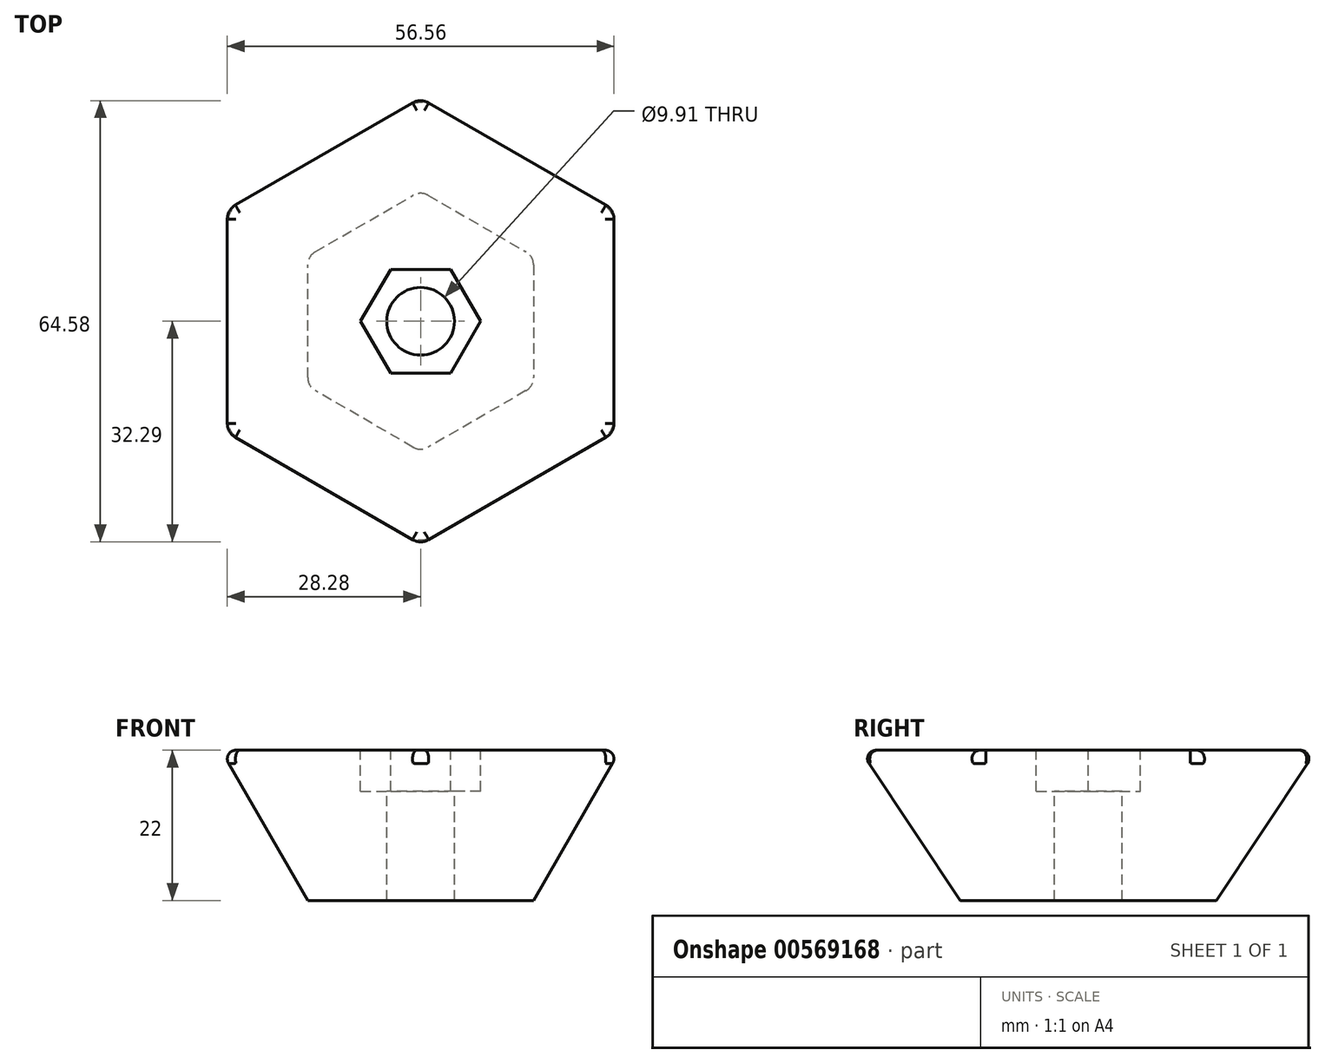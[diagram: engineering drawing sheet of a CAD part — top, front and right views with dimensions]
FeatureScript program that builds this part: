
annotation { "Feature Type Name" : "Feature", "Feature Type Description" : "" }
export const myFeature = defineFeature(function(context is Context, id is Id, definition is map)
    precondition{}
    {
        {
            var Q0;
            Q0=qCreatedBy(makeId("Top.planeOp"),FACE);
            var sketch = newSketch(context, id + "F0", { "sketchPlane" : qUnion([Q0])});
            skCircle(sketch, "E0.cCircle", {"center": v(0, 0) * mm, "radius": 29.21 * mm, "construction": true});
            skLineSegment(sketch, "E0.0", {"start": v(29.21, 16.86) * mm, "end": v(29.21, -16.86) * mm});
            skLineSegment(sketch, "E0.1", {"start": v(29.21, -16.86) * mm, "end": v(0, -33.73) * mm});
            skLineSegment(sketch, "E0.2", {"start": v(0, -33.73) * mm, "end": v(-29.2, -16.86) * mm});
            skLineSegment(sketch, "E0.3", {"start": v(-29.2, -16.86) * mm, "end": v(-29.21, 16.86) * mm});
            skLineSegment(sketch, "E0.4", {"start": v(-29.21, 16.86) * mm, "end": v(0, 33.73) * mm});
            skLineSegment(sketch, "E0.5", {"start": v(0, 33.73) * mm, "end": v(29.21, 16.86) * mm});
            skPoint(sketch, "E0.0.midPoint", {"position": v(29.21, 0) * mm});
            skSolve(sketch);
        }
        {
            var Q0;
            Q0 = qSketchRegion(id + "F0", true);
            extrude(context, id + "F1", {"entities" : qUnion([Q0]), "depth" : 22 * mm, "offsetDistance" : 25.4 * mm});
        }
        {
            var Q0;
            Q0=makeQuery(id+"F1.opExtrude","CAP_FACE",FACE,{"disambiguationData":[OSD([sQuery(id+"F0.wireOp",EDGE,"E0.0"),sQuery(id+"F0.wireOp",EDGE,"E0.1"),sQuery(id+"F0.wireOp",EDGE,"E0.2"),sQuery(id+"F0.wireOp",EDGE,"E0.3"),sQuery(id+"F0.wireOp",EDGE,"E0.4"),sQuery(id+"F0.wireOp",EDGE,"E0.5")])],"isStart":false});
            var sketch = newSketch(context, id + "F2", { "sketchPlane" : qUnion([Q0])});
            skCircle(sketch, "E1.cCircle", {"center": v(0, 0) * mm, "radius": 7.6 * mm, "construction": true});
            skLineSegment(sketch, "E1.0", {"start": v(-4.4, 7.6) * mm, "end": v(4.4, 7.6) * mm});
            skLineSegment(sketch, "E1.1", {"start": v(4.4, 7.6) * mm, "end": v(8.78, 0) * mm});
            skLineSegment(sketch, "E1.2", {"start": v(8.78, 0) * mm, "end": v(4.4, -7.6) * mm});
            skLineSegment(sketch, "E1.3", {"start": v(4.4, -7.6) * mm, "end": v(-4.4, -7.6) * mm});
            skLineSegment(sketch, "E1.4", {"start": v(-4.4, -7.6) * mm, "end": v(-8.78, 0) * mm});
            skLineSegment(sketch, "E1.5", {"start": v(-8.78, 0) * mm, "end": v(-4.4, 7.6) * mm});
            skPoint(sketch, "E1.0.midPoint", {"position": v(0, 7.6) * mm});
            skSolve(sketch);
        }
        {
            var Q0;
            Q0 = qSketchRegion(id + "F2", true);
            extrude(context, id + "F3", {"entities" : qUnion([Q0]), "operationType" : NewBodyOperationType.REMOVE, "oppositeDirection" : true, "depth" : 6 * mm, "offsetDistance" : 25.4 * mm});
        }
        {
            var Q0;
            Q0=makeQuery(id+"F3.boolean.opBoolean","COPY",FACE,{"derivedFrom":makeQuery(id+"F3.opExtrude","CAP_FACE",FACE,{"disambiguationData":[OSD([sQuery(id+"F2.wireOp",EDGE,"E1.0"),sQuery(id+"F2.wireOp",EDGE,"E1.1"),sQuery(id+"F2.wireOp",EDGE,"E1.2"),sQuery(id+"F2.wireOp",EDGE,"E1.3"),sQuery(id+"F2.wireOp",EDGE,"E1.4"),sQuery(id+"F2.wireOp",EDGE,"E1.5")])],"isStart":false})});
            var sketch = newSketch(context, id + "F4", { "sketchPlane" : qUnion([Q0])});
            skCircle(sketch, "E2", {"center": v(0, 0) * mm, "radius": 4.95 * mm});
            skSolve(sketch);
        }
        {
            var Q0;
            Q0 = qSketchRegion(id + "F4", true);
            extrude(context, id + "F5", {"entities" : qUnion([Q0]), "operationType" : NewBodyOperationType.REMOVE, "oppositeDirection" : true, "depth" : 22 * mm, "offsetDistance" : 25.4 * mm});
        }
        {
            var Q0;
            Q0=makeQuery(id+"F1.opExtrude","CAP_EDGE",EDGE,{"disambiguationData":[OSD([sQuery(id+"F0.wireOp",EDGE,"E0.2")])],"isStart":true});
            var Q1;
            Q1=makeQuery(id+"F1.opExtrude","CAP_EDGE",EDGE,{"disambiguationData":[OSD([sQuery(id+"F0.wireOp",EDGE,"E0.1")])],"isStart":true});
            var Q2;
            Q2=makeQuery(id+"F1.opExtrude","CAP_EDGE",EDGE,{"disambiguationData":[OSD([sQuery(id+"F0.wireOp",EDGE,"E0.3")])],"isStart":true});
            var Q3;
            Q3=makeQuery(id+"F1.opExtrude","CAP_EDGE",EDGE,{"disambiguationData":[OSD([sQuery(id+"F0.wireOp",EDGE,"E0.5")])],"isStart":true});
            var Q4;
            Q4=makeQuery(id+"F1.opExtrude","CAP_EDGE",EDGE,{"disambiguationData":[OSD([sQuery(id+"F0.wireOp",EDGE,"E0.4")])],"isStart":true});
            var Q5;
            Q5=makeQuery(id+"F1.opExtrude","CAP_EDGE",EDGE,{"disambiguationData":[OSD([sQuery(id+"F0.wireOp",EDGE,"E0.0")])],"isStart":true});
            chamfer(context, id + "F6", {"entities" : qUnion([Q0, Q1, Q2, Q3, Q4, Q5]), "chamferType" : ChamferType.OFFSET_ANGLE, "width" : 12.7 * mm, "oppositeDirection" : false, "angle" : 60 * degree, "tangentPropagation" : true});
        }
        {
            var Q0;
            {var subQ0=sQuery(id+"F0.wireOp",EDGE,"E0.2");Q0=makeQuery(id+"F6.opChamfer","BLEND_EDGE",EDGE,{"blendedFrom":[makeQuery(id+"F1.opExtrude","CAP_EDGE",EDGE,{"disambiguationData":[OSD([subQ0])],"isStart":true}),makeQuery(id+"F1.opExtrude","CAP_FACE",FACE,{"disambiguationData":[OSD([sQuery(id+"F0.wireOp",EDGE,"E0.0"),sQuery(id+"F0.wireOp",EDGE,"E0.1"),subQ0,sQuery(id+"F0.wireOp",EDGE,"E0.3"),sQuery(id+"F0.wireOp",EDGE,"E0.4"),sQuery(id+"F0.wireOp",EDGE,"E0.5")])],"isStart":false})],"blendedInto":[makeQuery(id+"F1.opExtrude","CAP_FACE",FACE,{"disambiguationData":[OSD([sQuery(id+"F0.wireOp",EDGE,"E0.0"),sQuery(id+"F0.wireOp",EDGE,"E0.1"),subQ0,sQuery(id+"F0.wireOp",EDGE,"E0.3"),sQuery(id+"F0.wireOp",EDGE,"E0.4"),sQuery(id+"F0.wireOp",EDGE,"E0.5")])],"isStart":false})]});}
            var Q1;
            {var subQ0=sQuery(id+"F0.wireOp",EDGE,"E0.3");Q1=makeQuery(id+"F6.opChamfer","BLEND_EDGE",EDGE,{"blendedFrom":[makeQuery(id+"F1.opExtrude","CAP_EDGE",EDGE,{"disambiguationData":[OSD([subQ0])],"isStart":true}),makeQuery(id+"F1.opExtrude","CAP_FACE",FACE,{"disambiguationData":[OSD([sQuery(id+"F0.wireOp",EDGE,"E0.0"),sQuery(id+"F0.wireOp",EDGE,"E0.1"),sQuery(id+"F0.wireOp",EDGE,"E0.2"),subQ0,sQuery(id+"F0.wireOp",EDGE,"E0.4"),sQuery(id+"F0.wireOp",EDGE,"E0.5")])],"isStart":false})],"blendedInto":[makeQuery(id+"F1.opExtrude","CAP_FACE",FACE,{"disambiguationData":[OSD([sQuery(id+"F0.wireOp",EDGE,"E0.0"),sQuery(id+"F0.wireOp",EDGE,"E0.1"),sQuery(id+"F0.wireOp",EDGE,"E0.2"),subQ0,sQuery(id+"F0.wireOp",EDGE,"E0.4"),sQuery(id+"F0.wireOp",EDGE,"E0.5")])],"isStart":false})]});}
            var Q2;
            {var subQ0=sQuery(id+"F0.wireOp",EDGE,"E0.4");Q2=makeQuery(id+"F6.opChamfer","BLEND_EDGE",EDGE,{"blendedFrom":[makeQuery(id+"F1.opExtrude","CAP_EDGE",EDGE,{"disambiguationData":[OSD([subQ0])],"isStart":true}),makeQuery(id+"F1.opExtrude","CAP_FACE",FACE,{"disambiguationData":[OSD([sQuery(id+"F0.wireOp",EDGE,"E0.0"),sQuery(id+"F0.wireOp",EDGE,"E0.1"),sQuery(id+"F0.wireOp",EDGE,"E0.2"),sQuery(id+"F0.wireOp",EDGE,"E0.3"),subQ0,sQuery(id+"F0.wireOp",EDGE,"E0.5")])],"isStart":false})],"blendedInto":[makeQuery(id+"F1.opExtrude","CAP_FACE",FACE,{"disambiguationData":[OSD([sQuery(id+"F0.wireOp",EDGE,"E0.0"),sQuery(id+"F0.wireOp",EDGE,"E0.1"),sQuery(id+"F0.wireOp",EDGE,"E0.2"),sQuery(id+"F0.wireOp",EDGE,"E0.3"),subQ0,sQuery(id+"F0.wireOp",EDGE,"E0.5")])],"isStart":false})]});}
            var Q3;
            {var subQ0=sQuery(id+"F0.wireOp",EDGE,"E0.5");Q3=makeQuery(id+"F6.opChamfer","BLEND_EDGE",EDGE,{"blendedFrom":[makeQuery(id+"F1.opExtrude","CAP_EDGE",EDGE,{"disambiguationData":[OSD([subQ0])],"isStart":true}),makeQuery(id+"F1.opExtrude","CAP_FACE",FACE,{"disambiguationData":[OSD([sQuery(id+"F0.wireOp",EDGE,"E0.0"),sQuery(id+"F0.wireOp",EDGE,"E0.1"),sQuery(id+"F0.wireOp",EDGE,"E0.2"),sQuery(id+"F0.wireOp",EDGE,"E0.3"),sQuery(id+"F0.wireOp",EDGE,"E0.4"),subQ0])],"isStart":false})],"blendedInto":[makeQuery(id+"F1.opExtrude","CAP_FACE",FACE,{"disambiguationData":[OSD([sQuery(id+"F0.wireOp",EDGE,"E0.0"),sQuery(id+"F0.wireOp",EDGE,"E0.1"),sQuery(id+"F0.wireOp",EDGE,"E0.2"),sQuery(id+"F0.wireOp",EDGE,"E0.3"),sQuery(id+"F0.wireOp",EDGE,"E0.4"),subQ0])],"isStart":false})]});}
            var Q4;
            {var subQ0=sQuery(id+"F0.wireOp",EDGE,"E0.0");Q4=makeQuery(id+"F6.opChamfer","BLEND_EDGE",EDGE,{"blendedFrom":[makeQuery(id+"F1.opExtrude","CAP_EDGE",EDGE,{"disambiguationData":[OSD([subQ0])],"isStart":true}),makeQuery(id+"F1.opExtrude","CAP_FACE",FACE,{"disambiguationData":[OSD([subQ0,sQuery(id+"F0.wireOp",EDGE,"E0.1"),sQuery(id+"F0.wireOp",EDGE,"E0.2"),sQuery(id+"F0.wireOp",EDGE,"E0.3"),sQuery(id+"F0.wireOp",EDGE,"E0.4"),sQuery(id+"F0.wireOp",EDGE,"E0.5")])],"isStart":false})],"blendedInto":[makeQuery(id+"F1.opExtrude","CAP_FACE",FACE,{"disambiguationData":[OSD([subQ0,sQuery(id+"F0.wireOp",EDGE,"E0.1"),sQuery(id+"F0.wireOp",EDGE,"E0.2"),sQuery(id+"F0.wireOp",EDGE,"E0.3"),sQuery(id+"F0.wireOp",EDGE,"E0.4"),sQuery(id+"F0.wireOp",EDGE,"E0.5")])],"isStart":false})]});}
            var Q5;
            {var subQ0=sQuery(id+"F0.wireOp",EDGE,"E0.1");Q5=makeQuery(id+"F6.opChamfer","BLEND_EDGE",EDGE,{"blendedFrom":[makeQuery(id+"F1.opExtrude","CAP_EDGE",EDGE,{"disambiguationData":[OSD([subQ0])],"isStart":true}),makeQuery(id+"F1.opExtrude","CAP_FACE",FACE,{"disambiguationData":[OSD([sQuery(id+"F0.wireOp",EDGE,"E0.0"),subQ0,sQuery(id+"F0.wireOp",EDGE,"E0.2"),sQuery(id+"F0.wireOp",EDGE,"E0.3"),sQuery(id+"F0.wireOp",EDGE,"E0.4"),sQuery(id+"F0.wireOp",EDGE,"E0.5")])],"isStart":false})],"blendedInto":[makeQuery(id+"F1.opExtrude","CAP_FACE",FACE,{"disambiguationData":[OSD([sQuery(id+"F0.wireOp",EDGE,"E0.0"),subQ0,sQuery(id+"F0.wireOp",EDGE,"E0.2"),sQuery(id+"F0.wireOp",EDGE,"E0.3"),sQuery(id+"F0.wireOp",EDGE,"E0.4"),sQuery(id+"F0.wireOp",EDGE,"E0.5")])],"isStart":false})]});}
            fillet(context, id + "F7", {"entities" : qUnion([Q0, Q1, Q2, Q3, Q4, Q5]), "radius" : 1.27 * mm, "tangentPropagation" : true, "allowEdgeOverflow" : false});
        }
        {
            var Q0;
            Q0=makeQuery(id+"F6.opChamfer","BLEND_EDGE",EDGE,{"blendedFrom":[makeQuery(id+"F1.opExtrude","CAP_EDGE",EDGE,{"disambiguationData":[OSD([sQuery(id+"F0.wireOp",EDGE,"E0.1")])],"isStart":true}),makeQuery(id+"F1.opExtrude","CAP_EDGE",EDGE,{"disambiguationData":[OSD([sQuery(id+"F0.wireOp",EDGE,"E0.2")])],"isStart":true})],"blendedInto":[]});
            var Q1;
            Q1=makeQuery(id+"F6.opChamfer","BLEND_EDGE",EDGE,{"blendedFrom":[makeQuery(id+"F1.opExtrude","CAP_EDGE",EDGE,{"disambiguationData":[OSD([sQuery(id+"F0.wireOp",EDGE,"E0.0")])],"isStart":true}),makeQuery(id+"F1.opExtrude","CAP_EDGE",EDGE,{"disambiguationData":[OSD([sQuery(id+"F0.wireOp",EDGE,"E0.1")])],"isStart":true})],"blendedInto":[]});
            var Q2;
            Q2=makeQuery(id+"F6.opChamfer","BLEND_EDGE",EDGE,{"blendedFrom":[makeQuery(id+"F1.opExtrude","CAP_EDGE",EDGE,{"disambiguationData":[OSD([sQuery(id+"F0.wireOp",EDGE,"E0.0")])],"isStart":true}),makeQuery(id+"F1.opExtrude","CAP_EDGE",EDGE,{"disambiguationData":[OSD([sQuery(id+"F0.wireOp",EDGE,"E0.5")])],"isStart":true})],"blendedInto":[]});
            var Q3;
            Q3=makeQuery(id+"F6.opChamfer","BLEND_EDGE",EDGE,{"blendedFrom":[makeQuery(id+"F1.opExtrude","CAP_EDGE",EDGE,{"disambiguationData":[OSD([sQuery(id+"F0.wireOp",EDGE,"E0.2")])],"isStart":true}),makeQuery(id+"F1.opExtrude","CAP_EDGE",EDGE,{"disambiguationData":[OSD([sQuery(id+"F0.wireOp",EDGE,"E0.3")])],"isStart":true})],"blendedInto":[]});
            var Q4;
            Q4=makeQuery(id+"F6.opChamfer","BLEND_EDGE",EDGE,{"blendedFrom":[makeQuery(id+"F1.opExtrude","CAP_EDGE",EDGE,{"disambiguationData":[OSD([sQuery(id+"F0.wireOp",EDGE,"E0.3")])],"isStart":true}),makeQuery(id+"F1.opExtrude","CAP_EDGE",EDGE,{"disambiguationData":[OSD([sQuery(id+"F0.wireOp",EDGE,"E0.4")])],"isStart":true})],"blendedInto":[]});
            var Q5;
            Q5=makeQuery(id+"F6.opChamfer","BLEND_EDGE",EDGE,{"blendedFrom":[makeQuery(id+"F1.opExtrude","CAP_EDGE",EDGE,{"disambiguationData":[OSD([sQuery(id+"F0.wireOp",EDGE,"E0.4")])],"isStart":true}),makeQuery(id+"F1.opExtrude","CAP_EDGE",EDGE,{"disambiguationData":[OSD([sQuery(id+"F0.wireOp",EDGE,"E0.5")])],"isStart":true})],"blendedInto":[]});
            fillet(context, id + "F8", {"entities" : qUnion([Q0, Q1, Q2, Q3, Q4, Q5]), "radius" : 2.54 * mm, "tangentPropagation" : true, "allowEdgeOverflow" : false});
        }
    });
